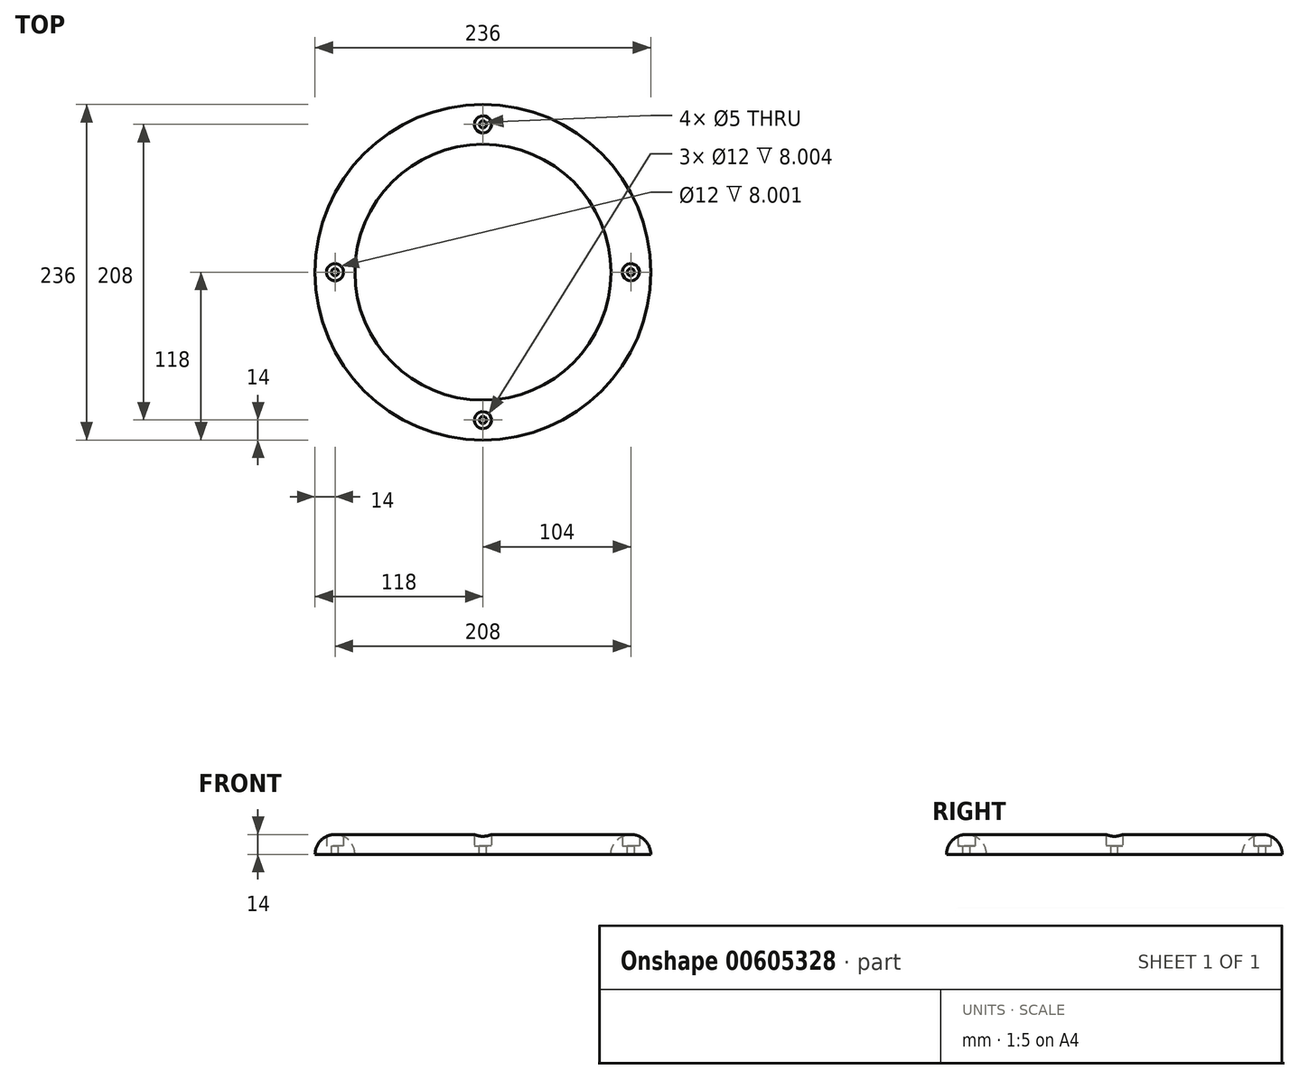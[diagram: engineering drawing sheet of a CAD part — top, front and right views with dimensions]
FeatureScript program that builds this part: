
annotation { "Feature Type Name" : "Feature", "Feature Type Description" : "" }
export const myFeature = defineFeature(function(context is Context, id is Id, definition is map)
    precondition{}
    {
        {
            var Q0;
            Q0=qCreatedBy(makeId("Front.planeOp"),FACE);
            var sketch = newSketch(context, id + "F0", { "sketchPlane" : qUnion([Q0])});
            skArc(sketch, "E0", {"start": v(-90, 0) * mm, "mid": v(-104, 14) * mm, "end": v(-118, 0) * mm});
            skLineSegment(sketch, "E1", {"start": v(-118, 0) * mm, "end": v(-90, 0) * mm});
            skLineSegment(sketch, "E2", {"start": v(0, 0) * mm, "end": v(0, 69.2) * mm});
            skSolve(sketch);
        }
        {
            var Q0;
            Q0=makeQuery(id+"F0.imprint","IMPRINT",FACE,{"disambiguationData":[TD([[makeQuery(id+"F0.imprint","IMPRINT",EDGE,{"derivedFrom":sQuery(id+"F0.wireOp",EDGE,"E0")}),1.0]])]});
            var Q1;
            Q1=sQuery(id+"F0.wireOp",EDGE,"E2");
            revolve(context, id + "F1", {"entities" : qUnion([Q0]), "axis" : qUnion([Q1]), "revolveType" : RevolveType.FULL});
        }
        {
            var Q0;
            Q0=qCreatedBy(makeId("Top.planeOp"),FACE);
            var sketch = newSketch(context, id + "F2", { "sketchPlane" : qUnion([Q0])});
            skCircle(sketch, "E3", {"center": v(0, -104) * mm, "radius": 6 * mm});
            skCircle(sketch, "E4.1.0", {"center": v(104, 0) * mm, "radius": 6 * mm});
            skCircle(sketch, "E4.2.0", {"center": v(0, 104) * mm, "radius": 6 * mm});
            skCircle(sketch, "E4.3.0", {"center": v(-104, 0) * mm, "radius": 6 * mm});
            skPoint(sketch, "E4.center", {"position": v(0, 0) * mm});
            skSolve(sketch);
        }
        {
            var Q0;
            Q0 = qSketchRegion(id + "F2", true);
            extrude(context, id + "F3", {"entities" : qUnion([Q0]), "operationType" : NewBodyOperationType.REMOVE, "oppositeDirection" : true, "depth" : -14 * mm, "offsetDistance" : 25 * mm});
        }
        {
            var Q0;
            Q0=qCreatedBy(makeId("Top.planeOp"),FACE);
            cPlane(context, id + "F4", {"entities" : qUnion([Q0]), "cplaneType" : CPlaneType.OFFSET, "offset" : 6 * mm, "width" : 150 * mm, "height" : 150 * mm});
        }
        {
            var Q0;
            Q0=qCreatedBy(id+"F4.planeOp",FACE);
            var sketch = newSketch(context, id + "F5", { "sketchPlane" : qUnion([Q0])});
            skCircle(sketch, "E5", {"center": v(104, 0) * mm, "radius": 6 * mm});
            skCircle(sketch, "E6.1.0", {"center": v(0, 104) * mm, "radius": 6 * mm});
            skCircle(sketch, "E6.2.0", {"center": v(-104, 0) * mm, "radius": 6 * mm});
            skCircle(sketch, "E6.3.0", {"center": v(0, -104) * mm, "radius": 6 * mm});
            skPoint(sketch, "E6.center", {"position": v(0, 0) * mm});
            skCircle(sketch, "E7", {"center": v(104, 0) * mm, "radius": 2.5 * mm});
            skCircle(sketch, "E8.1.0", {"center": v(0, 104) * mm, "radius": 2.5 * mm});
            skCircle(sketch, "E8.2.0", {"center": v(-104, 0) * mm, "radius": 2.5 * mm});
            skCircle(sketch, "E8.3.0", {"center": v(0, -104) * mm, "radius": 2.5 * mm});
            skSolve(sketch);
        }
        {
            var Q0;
            Q0=makeQuery(id+"F5.imprint","IMPRINT",FACE,{"disambiguationData":[TD([[makeQuery(id+"F5.imprint","IMPRINT",EDGE,{"derivedFrom":sQuery(id+"F5.wireOp",EDGE,"E5")}),1.0]])]});
            extrude(context, id + "F6", {"entities" : qUnion([Q0]), "operationType" : NewBodyOperationType.ADD, "depth" : -6 * mm, "offsetDistance" : 25 * mm});
        }
        {
            var Q0;
            Q0=makeQuery(id+"F1.opRevolve","SWEPT_BODY",BODY,{"disambiguationData":[OSD([sQuery(id+"F0.wireOp",EDGE,"E0"),sQuery(id+"F0.wireOp",EDGE,"E1")])]});
            var Q1;
            Q1=sQuery(id+"F0.wireOp",EDGE,"E2");
            circularPattern(context, id + "F7", {"operationType" : NewBodyOperationType.ADD, "entities" : qUnion([Q0]), "axis" : qUnion([Q1]), "angle" : 360 * degree, "instanceCount" : 4, "equalSpace" : true, "isCentered" : true});
        }
    });
